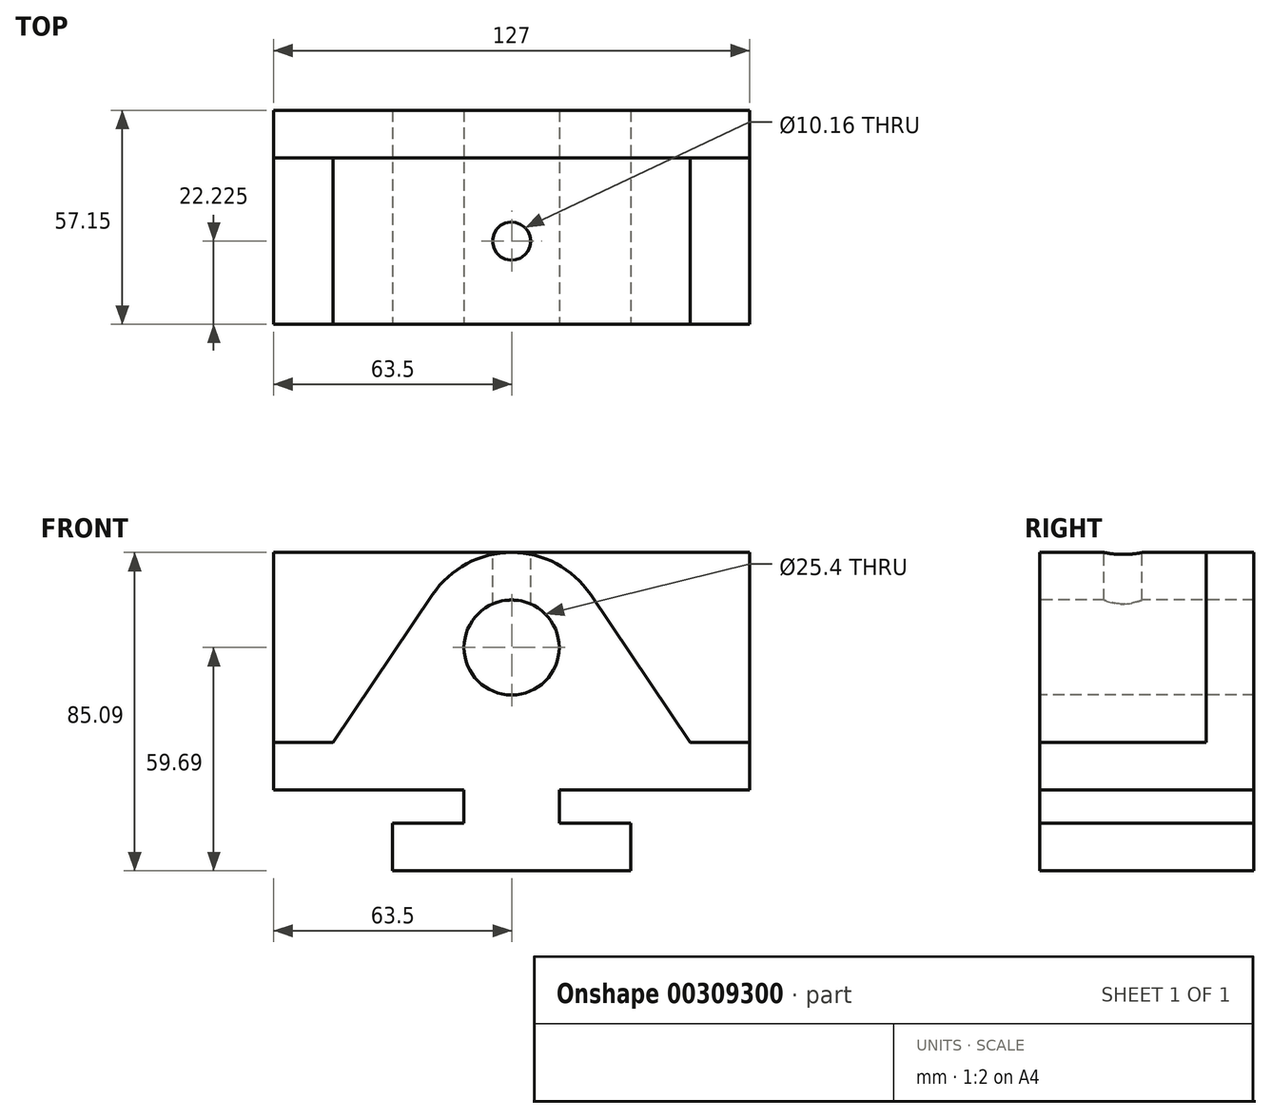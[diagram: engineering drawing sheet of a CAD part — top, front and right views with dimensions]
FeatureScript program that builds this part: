
annotation { "Feature Type Name" : "Feature", "Feature Type Description" : "" }
export const myFeature = defineFeature(function(context is Context, id is Id, definition is map)
    precondition{}
    {
        {
            var Q0;
            Q0=qCreatedBy(makeId("Front.planeOp"),FACE);
            var sketch = newSketch(context, id + "F0", { "sketchPlane" : qUnion([Q0])});
            skLineSegment(sketch, "E0", {"start": v(0, 0) * mm, "end": v(0, 85.1) * mm});
            skLineSegment(sketch, "E1", {"start": v(0, 85.1) * mm, "end": v(127, 85.1) * mm});
            skLineSegment(sketch, "E2", {"start": v(127, 85.1) * mm, "end": v(127, 0) * mm});
            skLineSegment(sketch, "E3", {"start": v(127, 0) * mm, "end": v(0, 0) * mm});
            skSolve(sketch);
        }
        {
            var Q0;
            Q0 = qSketchRegion(id + "F0", true);
            extrude(context, id + "F1", {"entities" : qUnion([Q0]), "depth" : 57.15 * mm});
        }
        {
            var Q0;
            Q0=makeQuery(id+"F1.opExtrude","CAP_FACE",FACE,{"disambiguationData":[OSD([sQuery(id+"F0.wireOp",EDGE,"E0"),sQuery(id+"F0.wireOp",EDGE,"E1"),sQuery(id+"F0.wireOp",EDGE,"E2"),sQuery(id+"F0.wireOp",EDGE,"E3")])],"isStart":false});
            var sketch = newSketch(context, id + "F2", { "sketchPlane" : qUnion([Q0])});
            skLineSegment(sketch, "E4", {"start": v(63.5, 111.11) * mm, "end": v(63.5, -7.39) * mm, "construction": true});
            skPoint(sketch, "E4.startSnap0", {"position": v(63.5, 85.1) * mm});
            skLineSegment(sketch, "E5", {"start": v(63.5, 0) * mm, "end": v(31.75, 0) * mm});
            skLineSegment(sketch, "E6", {"start": v(31.75, 0) * mm, "end": v(31.75, 12.7) * mm});
            skLineSegment(sketch, "E7", {"start": v(31.75, 12.7) * mm, "end": v(50.8, 12.7) * mm});
            skLineSegment(sketch, "E8", {"start": v(50.8, 12.7) * mm, "end": v(50.8, 21.6) * mm});
            skLineSegment(sketch, "E9", {"start": v(50.8, 21.6) * mm, "end": v(0, 21.59) * mm});
            skLineSegment(sketch, "E10", {"start": v(0, 21.59) * mm, "end": v(0, 34.3) * mm});
            skLineSegment(sketch, "E11", {"start": v(0, 34.3) * mm, "end": v(15.88, 34.3) * mm});
            skLineSegment(sketch, "E12", {"start": v(15.87, 34.29) * mm, "end": v(42.4, 73.84) * mm});
            skLineSegment(sketch, "E13.MirrorCS", {"start": v(63.5, 0) * mm, "end": v(95.25, 0) * mm});
            skLineSegment(sketch, "E14.MirrorCS", {"start": v(95.25, 0) * mm, "end": v(95.25, 12.7) * mm});
            skLineSegment(sketch, "E15.MirrorCS", {"start": v(95.25, 12.7) * mm, "end": v(76.2, 12.7) * mm});
            skLineSegment(sketch, "E16.MirrorCS", {"start": v(76.2, 12.7) * mm, "end": v(76.2, 21.6) * mm});
            skLineSegment(sketch, "E17.MirrorCS", {"start": v(76.2, 21.6) * mm, "end": v(127, 21.59) * mm});
            skLineSegment(sketch, "E18.MirrorCS", {"start": v(127, 21.59) * mm, "end": v(127, 34.3) * mm});
            skLineSegment(sketch, "E19.MirrorCS", {"start": v(127, 34.3) * mm, "end": v(111.13, 34.3) * mm});
            skLineSegment(sketch, "E20.MirrorCS", {"start": v(111.13, 34.3) * mm, "end": v(84.6, 73.84) * mm});
            skArc(sketch, "E21", {"start": v(84.6, 73.84) * mm, "mid": v(63.5, 85.1) * mm, "end": v(42.4, 73.84) * mm});
            skCircle(sketch, "E22", {"center": v(63.5, 59.7) * mm, "radius": 12.7 * mm});
            skSolve(sketch);
        }
        {
            var Q0;
            {var subQ4=sQuery(id+"F2.wireOp",EDGE,"E6");Q0=makeQuery(id+"F2.imprint","IMPRINT",FACE,{"disambiguationData":[TD([[makeQuery(id+"F2.imprint","IMPRINT",EDGE,{"derivedFrom":subQ4}),1.0]])]});}
            var Q1;
            {var subQ1=sQuery(id+"F2.wireOp",EDGE,"E14.MirrorCS");Q1=makeQuery(id+"F2.imprint","IMPRINT",FACE,{"disambiguationData":[TD([[makeQuery(id+"F2.imprint","IMPRINT",EDGE,{"derivedFrom":subQ1}),-1.0]])]});}
            var Q2;
            Q2=makeQuery(id+"F2.imprint","IMPRINT",FACE,{"disambiguationData":[TD([[makeQuery(id+"F2.imprint","IMPRINT",EDGE,{"derivedFrom":sQuery(id+"F2.wireOp",EDGE,"E22")}),1.0]])]});
            extrude(context, id + "F3", {"entities" : qUnion([Q0, Q1, Q2]), "operationType" : NewBodyOperationType.REMOVE, "endBound" : BoundingType.THROUGH_ALL, "oppositeDirection" : true, "depth" : 25.4 * mm});
        }
        {
            var Q0;
            {var subQ6=sQuery(id+"F2.wireOp",EDGE,"E19.MirrorCS");Q0=makeQuery(id+"F2.imprint","IMPRINT",FACE,{"disambiguationData":[TD([[makeQuery(id+"F2.imprint","IMPRINT",EDGE,{"derivedFrom":subQ6}),-1.0]])]});}
            var Q1;
            {var subQ3=sQuery(id+"F2.wireOp",EDGE,"E11");Q1=makeQuery(id+"F2.imprint","IMPRINT",FACE,{"disambiguationData":[TD([[makeQuery(id+"F2.imprint","IMPRINT",EDGE,{"derivedFrom":subQ3}),1.0]])]});}
            extrude(context, id + "F4", {"entities" : qUnion([Q0, Q1]), "operationType" : NewBodyOperationType.REMOVE, "oppositeDirection" : true, "depth" : 44.45 * mm});
        }
        {
            var Q0;
            Q0=makeQuery(id+"F1.opExtrude","SWEPT_FACE",FACE,{"disambiguationData":[OSD([sQuery(id+"F0.wireOp",EDGE,"E1")])]});
            var sketch = newSketch(context, id + "F5", { "sketchPlane" : qUnion([Q0])});
            skCircle(sketch, "E23", {"center": v(63.5, -34.93) * mm, "radius": 5.08 * mm});
            skSolve(sketch);
        }
        {
            var Q0;
            Q0=makeQuery(id+"F5.imprint","IMPRINT",FACE,{"disambiguationData":[TD([[makeQuery(id+"F5.imprint","IMPRINT",EDGE,{"derivedFrom":sQuery(id+"F5.wireOp",EDGE,"E23")}),1.0]])]});
            extrude(context, id + "F6", {"entities" : qUnion([Q0]), "operationType" : NewBodyOperationType.REMOVE, "endBound" : BoundingType.UP_TO_NEXT, "oppositeDirection" : true, "depth" : 25.4 * mm});
        }
    });
